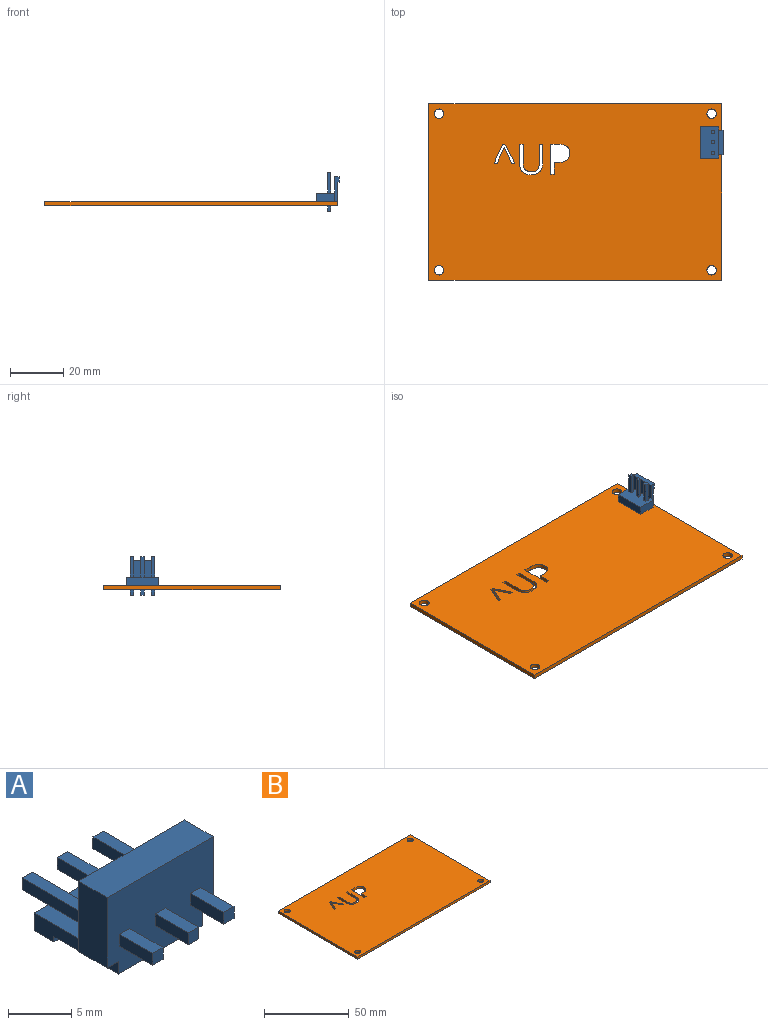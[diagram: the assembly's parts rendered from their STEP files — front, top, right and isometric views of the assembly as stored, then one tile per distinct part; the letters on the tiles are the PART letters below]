
ASSEMBLY  parts=2 mates=1
PART A: 44 faces, bbox 11.8x14.6x8.5 mm
  f0: plane 7.7x1.14mm, normal (0,0,1), area 8.8mm2, adj f1,f2,f3,f4
  f1: plane 11.82x6.8mm, normal (0,1,0), area 76.5mm2, adj f0,f2,f4,f5,f6,f7,f8,f9
  f2: plane 7.7x1.14mm, normal (-1,0,0), area 8.8mm2, adj f0,f1,f3,f7
  f3: plane 1.14x1.14mm, normal (0,1,0), area 1.3mm2, adj f0,f2,f4,f7
  f4: plane 7.7x1.14mm, normal (1,0,0), area 8.8mm2, adj f0,f1,f3,f7
  f5: plane 7.7x1.14mm, normal (0,0,-1), area 8.8mm2, adj f1,f11,f19,f20
  f6: plane 6.8x3.2mm, normal (-1,0,0), area 21.8mm2, adj f1,f9,f17,f21
  f7: plane 7.7x1.14mm, normal (0,0,-1), area 8.8mm2, adj f1,f2,f3,f4
  f8: plane 6.8x3.2mm, normal (1,0,0), area 21.8mm2, adj f1,f9,f10,f21
  f9: plane 11.82x3.2mm, normal (0,0,1), area 37.8mm2, adj f1,f6,f8,f21
  f10: plane 3.2x1.25mm, normal (0,0,-1), area 4mm2, adj f1,f8,f21,f22
  f11: plane 7.7x1.14mm, normal (-1,0,0), area 8.8mm2, adj f1,f5,f18,f20
  f12: plane 9.32x6.2mm, normal (0,0,1), area 57.8mm2, adj f1,f22,f23,f24
  f13: plane 7.7x1.14mm, normal (-1,0,0), area 8.8mm2, adj f1,f15,f16,f25
  f14: plane 7.7x1.14mm, normal (1,0,0), area 8.8mm2, adj f1,f15,f16,f25
  f15: plane 7.7x1.14mm, normal (0,0,-1), area 8.8mm2, adj f1,f13,f14,f25
  f16: plane 7.7x1.14mm, normal (0,0,1), area 8.8mm2, adj f1,f13,f14,f25
  f17: plane 3.2x1.25mm, normal (0,0,-1), area 4mm2, adj f1,f6,f21,f24
  f18: plane 7.7x1.14mm, normal (0,0,1), area 8.8mm2, adj f1,f11,f19,f20
  f19: plane 7.7x1.14mm, normal (1,0,0), area 8.8mm2, adj f1,f5,f18,f20
  f20: plane 1.14x1.14mm, normal (0,1,0), area 1.3mm2, adj f5,f11,f18,f19
  f21: plane 11.82x8mm, normal (0,-1,0), area 87.7mm2, adj f6,f8,f9,f10,f17,f22,f24,f26
  f22: plane 9.4x1.7mm, normal (1,0,0), area 12.4mm2, adj f10,f12,f21,f23,f30,f39,f40
  f23: plane 9.32x1.7mm, normal (0,1,0), area 15.8mm2, adj f12,f22,f24,f40
  f24: plane 9.4x1.7mm, normal (-1,0,0), area 12.4mm2, adj f12,f17,f21,f23,f30,f39,f40
  f25: plane 1.14x1.14mm, normal (0,1,0), area 1.3mm2, adj f13,f14,f15,f16
  f26: plane 3.7x1.14mm, normal (0,0,-1), area 4.2mm2, adj f21,f28,f31,f41
  f27: plane 3.7x1.14mm, normal (1,0,0), area 4.2mm2, adj f21,f34,f38,f42
  f28: plane 3.7x1.14mm, normal (-1,0,0), area 4.2mm2, adj f21,f26,f36,f41
  f29: plane 3.7x1.14mm, normal (-1,0,0), area 4.2mm2, adj f21,f34,f38,f42
  f30: plane 9.32x7.2mm, normal (0,0,-1), area 67.1mm2, adj f21,f22,f24,f39
  f31: plane 3.7x1.14mm, normal (1,0,0), area 4.2mm2, adj f21,f26,f36,f41
  f32: plane 3.7x1.14mm, normal (0,0,-1), area 4.2mm2, adj f21,f33,f35,f43
  f33: plane 3.7x1.14mm, normal (-1,0,0), area 4.2mm2, adj f21,f32,f37,f43
  f34: plane 3.7x1.14mm, normal (0,0,-1), area 4.2mm2, adj f21,f27,f29,f42
  f35: plane 3.7x1.14mm, normal (1,0,0), area 4.2mm2, adj f21,f32,f37,f43
  f36: plane 3.7x1.14mm, normal (0,0,1), area 4.2mm2, adj f21,f28,f31,f41
  f37: plane 3.7x1.14mm, normal (0,0,1), area 4.2mm2, adj f21,f33,f35,f43
  f38: plane 3.7x1.14mm, normal (0,0,1), area 4.2mm2, adj f21,f27,f29,f42
  f39: plane 9.32x0.5mm, normal (0,-1,0), area 4.7mm2, adj f22,f24,f30,f40
  f40: plane 9.32x2.2mm, normal (0,0,-1), area 20.5mm2, adj f22,f23,f24,f39
  f41: plane 1.14x1.14mm, normal (0,-1,0), area 1.3mm2, adj f26,f28,f31,f36
  f42: plane 1.14x1.14mm, normal (0,-1,0), area 1.3mm2, adj f27,f29,f34,f38
  f43: plane 1.14x1.14mm, normal (0,-1,0), area 1.3mm2, adj f32,f33,f35,f37
PART B: 39 faces, bbox 110.5x66.7x1.6 mm
  f0: plane 1.6x1.18mm, normal (0,1,0), area 1.9mm2, adj f1,f32,f33,f34
  f1: plane 7.16x3.37mm, normal (0.9,-0.43,0), area 12.7mm2, adj f0,f2,f33,f34
  f2: plane 1.6x0.77mm, normal (0,-1,0), area 1.2mm2, adj f1,f3,f33,f34
  f3: plane 7.16x3.7mm, normal (-0.89,-0.46,0), area 12.9mm2, adj f2,f4,f33,f34
  f4: plane 1.6x1.18mm, normal (0,1,0), area 1.9mm2, adj f3,f5,f33,f34
  f5: plane 5.79x2.89mm, normal (0.89,0.45,0), area 10.3mm2, adj f4,f32,f33,f34
  f6: plane 1.6x1.32mm, normal (0,-1,0), area 2.1mm2, adj f7,f29,f33,f34
  f7: plane 7.35x1.6mm, normal (-1,0,0), area 11.8mm2, adj f6,f8,f33,f34
  f8: extruded ~3.06x1.6mm, area 5.4mm2, adj f7,f9,f33,f34
  f9: extruded ~3.22x1.6mm, area 5.6mm2, adj f8,f10,f33,f34
  f10: extruded ~3.17x1.6mm, area 5.5mm2, adj f9,f11,f33,f34
  f11: extruded ~3.08x1.6mm, area 5.4mm2, adj f10,f12,f33,f34
  f12: plane 7.32x1.6mm, normal (1,0,0), area 11.7mm2, adj f11,f13,f33,f34
  f13: plane 1.6x1.32mm, normal (0,-1,0), area 2.1mm2, adj f12,f14,f33,f34
  f14: plane 7.41x1.6mm, normal (-1,0,0), area 11.9mm2, adj f13,f15,f33,f34
  f15: extruded ~2.18x1.6mm, area 3.8mm2, adj f14,f16,f33,f34
  f16: extruded ~2.28x1.6mm, area 4mm2, adj f15,f17,f33,f34
  f17: extruded ~2.21x1.6mm, area 3.8mm2, adj f16,f18,f33,f34
  f18: extruded ~2.2x1.6mm, area 3.8mm2, adj f17,f29,f33,f34
  f19: extruded ~4.26x3.31mm, area 9.9mm2, adj f20,f30,f33,f34
  f20: extruded ~2.65x1.6mm, area 4.8mm2, adj f19,f21,f33,f34
  f21: extruded ~3.37x1.6mm, area 5.7mm2, adj f20,f22,f33,f34
  f22: plane 1.6x1.34mm, normal (0,1,0), area 2.1mm2, adj f21,f23,f33,f34
  f23: plane 4.47x1.6mm, normal (-1,0,0), area 7.1mm2, adj f22,f24,f33,f34
  f24: plane 1.6x1.32mm, normal (0,1,0), area 2.1mm2, adj f23,f25,f33,f34
  f25: plane 11.36x1.6mm, normal (1,0,0), area 18.2mm2, adj f24,f30,f33,f34
  f26: plane 66.68x1.6mm, normal (-1,0,0), area 106.7mm2, adj f27,f31,f33,f34
  f27: plane 110.49x1.6mm, normal (0,-1,0), area 176.8mm2, adj f26,f28,f33,f34
  f28: plane 66.68x1.6mm, normal (1,0,0), area 106.7mm2, adj f27,f31,f33,f34
  f29: plane 7.4x1.6mm, normal (1,0,0), area 11.8mm2, adj f6,f18,f33,f34
  f30: plane 2.95x1.6mm, normal (0,-1,0), area 4.7mm2, adj f19,f25,f33,f34
  f31: plane 110.49x1.6mm, normal (0,1,0), area 176.8mm2, adj f26,f28,f33,f34
  f32: plane 5.79x2.6mm, normal (-0.91,0.41,0), area 10.1mm2, adj f0,f5,f33,f34
  f33: plane 110.49x66.68mm, normal (0,0,1), area 7227mm2, adj f0,f1,f2,f3,f4,f5,f6,f7
  f34: plane 110.49x66.68mm, normal (0,0,-1), area 7227mm2, adj f0,f1,f2,f3,f4,f5,f6,f7
  f35: cylinder r=1.8mm len=3.6mm, axis (0,0,-1), area 18.1mm2, adj f33,f34
  f36: cylinder r=1.8mm len=3.6mm, axis (0,0,-1), area 18.1mm2, adj f33,f34
  f37: cylinder r=1.8mm len=3.6mm, axis (0,0,-1), area 18.1mm2, adj f33,f34
  f38: cylinder r=1.8mm len=3.6mm, axis (0,0,-1), area 18.1mm2, adj f33,f34
PLACE A rot(axis=(0.58,-0.58,-0.58),120deg) t=(106.74,52.01,1.6)mm
PLACE B at identity fixed
MATE fastened A.f21 <-> B.f33  axis (0,0,-1) through (110.49,56.67,1.6)mm
